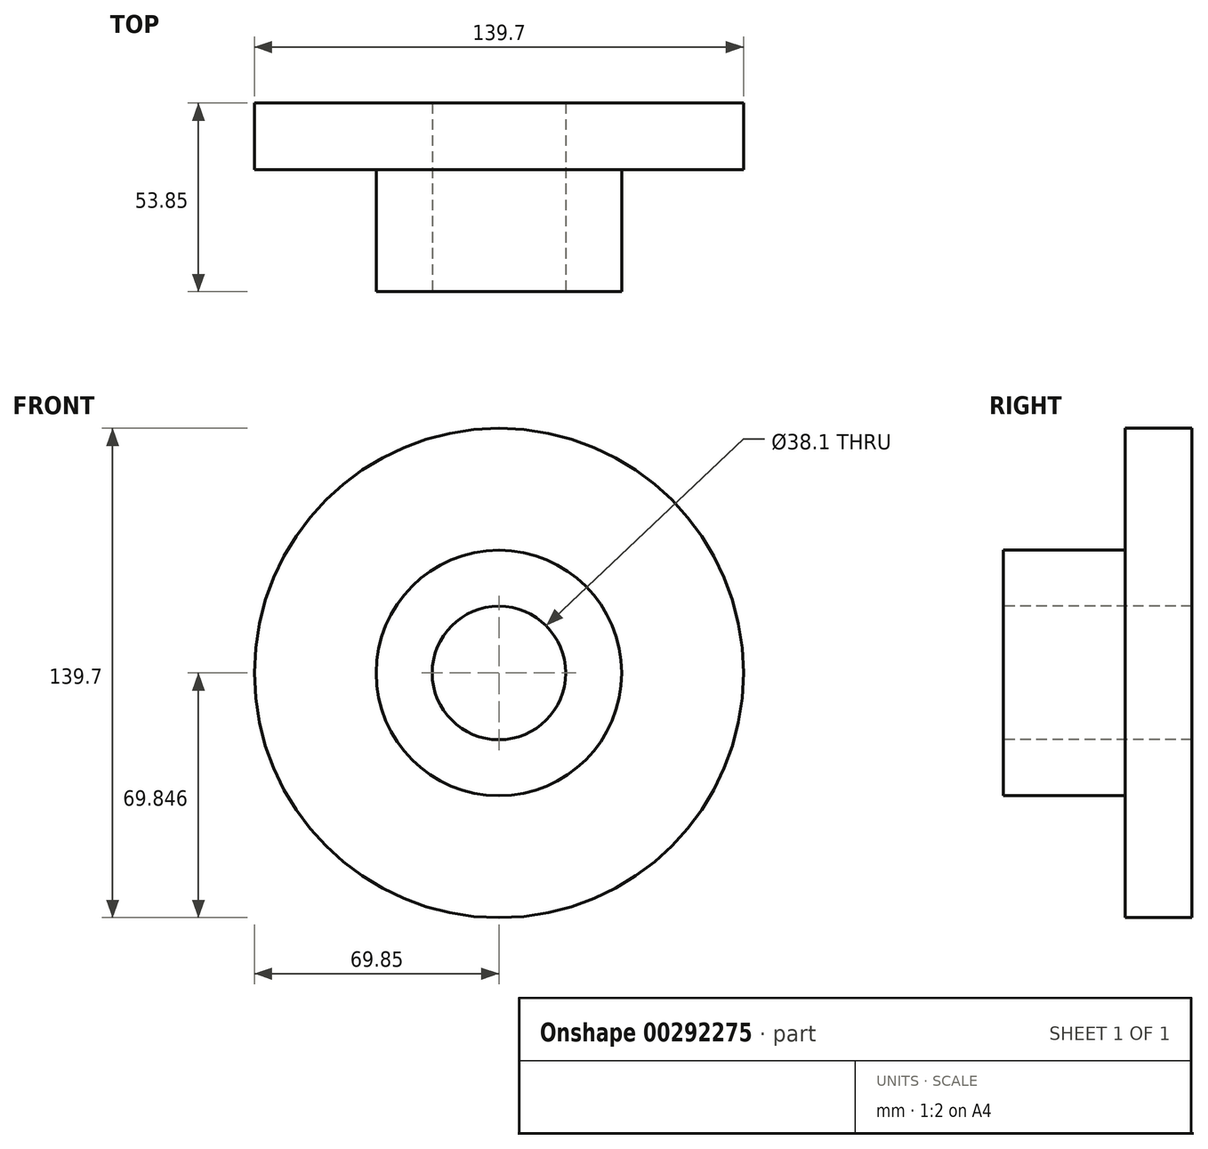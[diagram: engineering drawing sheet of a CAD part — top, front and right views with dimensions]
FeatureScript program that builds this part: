
annotation { "Feature Type Name" : "Feature", "Feature Type Description" : "" }
export const myFeature = defineFeature(function(context is Context, id is Id, definition is map)
    precondition{}
    {
        {
            var Q0;
            Q0=qCreatedBy(makeId("Front.planeOp"),FACE);
            var sketch = newSketch(context, id + "F0", { "sketchPlane" : qUnion([Q0])});
            skCircle(sketch, "E0", {"center": v(-39.63, -28.48) * mm, "radius": 69.85 * mm});
            skSolve(sketch);
        }
        {
            var Q0;
            Q0=makeQuery(id+"F0.imprint","IMPRINT",FACE,{"disambiguationData":[TD([[makeQuery(id+"F0.imprint","IMPRINT",EDGE,{"derivedFrom":sQuery(id+"F0.wireOp",EDGE,"E0")}),1.0]])]});
            extrude(context, id + "F1", {"entities" : qUnion([Q0]), "depth" : 19.05 * mm});
        }
        {
            var Q0;
            Q0=makeQuery(id+"F1.opExtrude","CAP_FACE",FACE,{"disambiguationData":[OSD([sQuery(id+"F0.wireOp",EDGE,"E0")])],"isStart":false});
            var sketch = newSketch(context, id + "F2", { "sketchPlane" : qUnion([Q0])});
            skCircle(sketch, "E1", {"center": v(-39.63, -28.48) * mm, "radius": 35.05 * mm});
            skSolve(sketch);
        }
        {
            var Q0;
            Q0 = qSketchRegion(id + "F2", true);
            extrude(context, id + "F3", {"entities" : qUnion([Q0]), "operationType" : NewBodyOperationType.ADD, "depth" : 34.8 * mm});
        }
        {
            var Q0;
            Q0=makeQuery(id+"F3.opExtrude","CAP_FACE",FACE,{"disambiguationData":[OSD([sQuery(id+"F2.wireOp",EDGE,"E1")])],"isStart":false});
            var sketch = newSketch(context, id + "F4", { "sketchPlane" : qUnion([Q0])});
            skCircle(sketch, "E2", {"center": v(-39.63, -28.48) * mm, "radius": 19.05 * mm});
            skSolve(sketch);
        }
        {
            var Q0;
            Q0=makeQuery(id+"F4.imprint","IMPRINT",FACE,{"disambiguationData":[TD([[makeQuery(id+"F4.imprint","IMPRINT",EDGE,{"derivedFrom":sQuery(id+"F4.wireOp",EDGE,"E2")}),1.0]])]});
            extrude(context, id + "F5", {"entities" : qUnion([Q0]), "operationType" : NewBodyOperationType.REMOVE, "endBound" : BoundingType.THROUGH_ALL, "oppositeDirection" : true, "depth" : 25.4 * mm});
        }
    });
